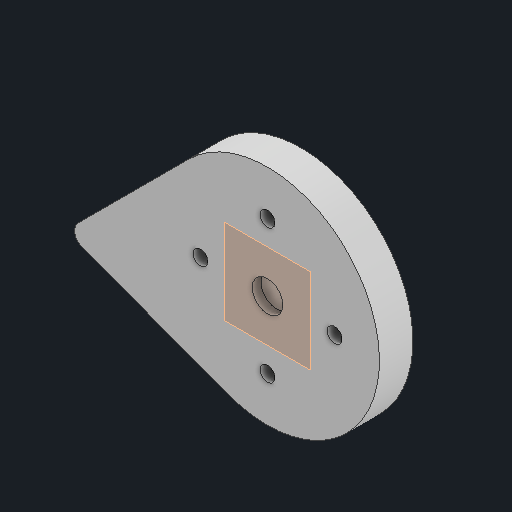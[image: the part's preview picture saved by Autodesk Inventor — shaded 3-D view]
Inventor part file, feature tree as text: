
AUTODESK INVENTOR PART (.ipt)
format: ipt  version: 2024.1 (Build 281209000, 209)  size: 158,208 bytes
history: native  units: in
note: dims shown in document units (in); Inventor stores cm internally (conversion verified against a paired STEP export)
features: other x3, sketch x1, plane x1
ambient origin geometry x8: Origin, YZ Plane, XZ Plane, XY Plane, X Axis, Y Axis, Z Axis, Center Point
bodies: Solid1 (feature_tree)
feature tree (5):
  other  "WeightBearingMount.ipt"
  other  "Solid1::WeightBearingMount.ipt"
  other  "TaggingFeature1"
  sketch  "Sketch1"  dims[d0=0.3937in]
  plane  "Work Plane1"
